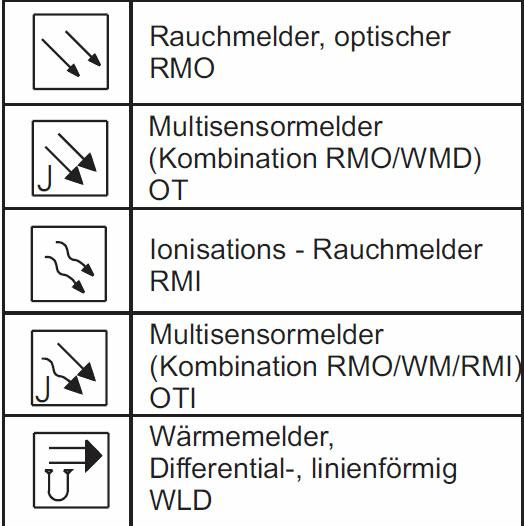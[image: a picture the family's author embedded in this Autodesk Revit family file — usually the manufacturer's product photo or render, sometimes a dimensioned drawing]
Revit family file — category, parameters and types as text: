
# Revit family: IQ8Quad
name_source: partatom
category: Fire Alarm Devices
revit_build: Autodesk Revit 2014 (Build: 20130308_1515(x64)
units: mm (PartAtom-declared; Revit-internal decimal feet)

## types (13) — shared parameters
Manufacturer = Esser by Honeywell
URL = http://www.esser-systems.com
content_date_modified = 16.06.2015
content_version = 1.0
h1 = 62 mm  [stored 0.203412 ft]
l1 = 117 mm  [stored 0.383858 ft]
material = White
material 2 = Transparant

## per-type parameters (varying)
| type | Model | article number |
| Optical Smoke Detector | IQ8Quad Optical Smoke Detector | 802371 |
| O2T Multisensor Detector | O2T multisensor fire detector IQ8Quad with isolator | 802374 |
| OT Multisensor Detector | OT multisensor fire detector IQ8Quad with isolator | 802373 |
| OT-blue Multisensor Detector | OTblue multisensor fire detector IQ8Quad with isolator | 802375 |
| OTblue-LKM multisensor Fire Detector | OTblue-LKM multisensor fire detector IQ8Quad with isolator | 802379 |
| Fixed heat detector | Fixed heat detector IQ8Quad with isolator | 802171 |
| OTG multisensor Fire Detector (CO) | OTG multisensor fire detector (CO) IQ8Quad with isolator | 802473 |
| O2T/So multisensor Fire Detector | O2T/So multisensor fire detector IQ8Quad with isolator | 802384 |
| O/So optical Smoke Detector | O/So optical smoke detector IQ8Quad with isolator | 802382 |
| O2T/FSp multisensor Fire Detector | O2T/FSp multisensor fire detector IQ8Quad with isolator | 802385 |
| O2T/Sp multisensor Fire Detector | O2T/Sp multisensor fire detector IQ8Quad with isolator | 802386 |
| O2T/F multisensor Fire Detector | O2T/F multisensor fire detector IQ8Quad with isolator | 802383 |
| Rate-of-rise Heat Detector | Rate-of-rise heat detector IQ8Quad with isolator | 802271 |

note: [stored X ft] marks values corroborated as IEEE doubles in the binary element streams (Revit-internal decimal feet)

## geometry (parser evidence)
native form markers: Sweep x8
no freeform markers — native parametric forms only
